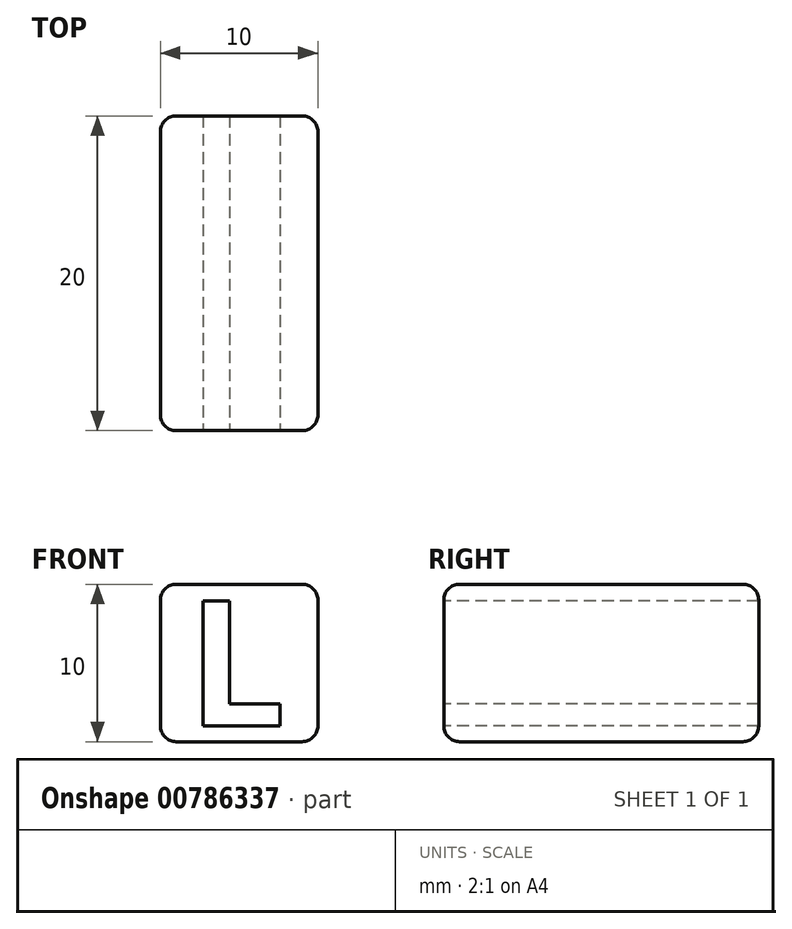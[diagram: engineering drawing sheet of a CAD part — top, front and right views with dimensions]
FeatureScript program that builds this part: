
annotation { "Feature Type Name" : "Feature", "Feature Type Description" : "" }
export const myFeature = defineFeature(function(context is Context, id is Id, definition is map)
    precondition{}
    {
        {
            var Q0;
            Q0=qCreatedBy(makeId("Front.planeOp"),FACE);
            var sketch = newSketch(context, id + "F0", { "sketchPlane" : qUnion([Q0])});
            skLineSegment(sketch, "E0.bottom", {"start": v(0, 0) * mm, "end": v(10, 0) * mm});
            skLineSegment(sketch, "E0.top", {"start": v(0, 10) * mm, "end": v(10, 10) * mm});
            skLineSegment(sketch, "E0.left", {"start": v(0, 0) * mm, "end": v(0, 10) * mm});
            skLineSegment(sketch, "E0.right", {"start": v(10, 0) * mm, "end": v(10, 10) * mm});
            skSolve(sketch);
        }
        {
            var Q0;
            Q0 = qSketchRegion(id + "F0", true);
            extrude(context, id + "F1", {"entities" : qUnion([Q0]), "depth" : 20 * mm, "offsetDistance" : 25 * mm});
        }
        {
            var Q0;
            Q0=makeQuery(id+"F1.opExtrude","SWEPT_FACE",FACE,{"disambiguationData":[OSD([sQuery(id+"F0.wireOp",EDGE,"E0.top")])]});
            var Q1;
            Q1=makeQuery(id+"F1.opExtrude","SWEPT_FACE",FACE,{"disambiguationData":[OSD([sQuery(id+"F0.wireOp",EDGE,"E0.right")])]});
            var Q2;
            Q2=makeQuery(id+"F1.opExtrude","SWEPT_FACE",FACE,{"disambiguationData":[OSD([sQuery(id+"F0.wireOp",EDGE,"E0.bottom")])]});
            var Q3;
            Q3=makeQuery(id+"F1.opExtrude","SWEPT_FACE",FACE,{"disambiguationData":[OSD([sQuery(id+"F0.wireOp",EDGE,"E0.left")])]});
            fillet(context, id + "F2", {"entities" : qUnion([Q0, Q1, Q2, Q3]), "radius" : 1 * mm, "tangentPropagation" : true, "allowEdgeOverflow" : false});
        }
        {
            var Q0;
            Q0=makeQuery(id+"F1.opExtrude","CAP_FACE",FACE,{"disambiguationData":[OSD([sQuery(id+"F0.wireOp",EDGE,"E0.bottom"),sQuery(id+"F0.wireOp",EDGE,"E0.top"),sQuery(id+"F0.wireOp",EDGE,"E0.left"),sQuery(id+"F0.wireOp",EDGE,"E0.right")])],"isStart":false});
            var sketch = newSketch(context, id + "F3", { "sketchPlane" : qUnion([Q0])});
            skText(sketch, "E1", { "text": "L", "fontName": "OpenSans-Bold.ttf"});
            const initialGuessF3  = {"E1": [0.0017, 0.001, 1, 0, 0.008]};
            skSetInitialGuess(sketch, initialGuessF3);
            skSolve(sketch);
        }
        {
            var Q0;
            Q0 = qSketchRegion(id + "F3", true);
            extrude(context, id + "F4", {"entities" : qUnion([Q0]), "operationType" : NewBodyOperationType.REMOVE, "oppositeDirection" : true, "depth" : 20 * mm, "offsetDistance" : 25 * mm});
        }
    });
